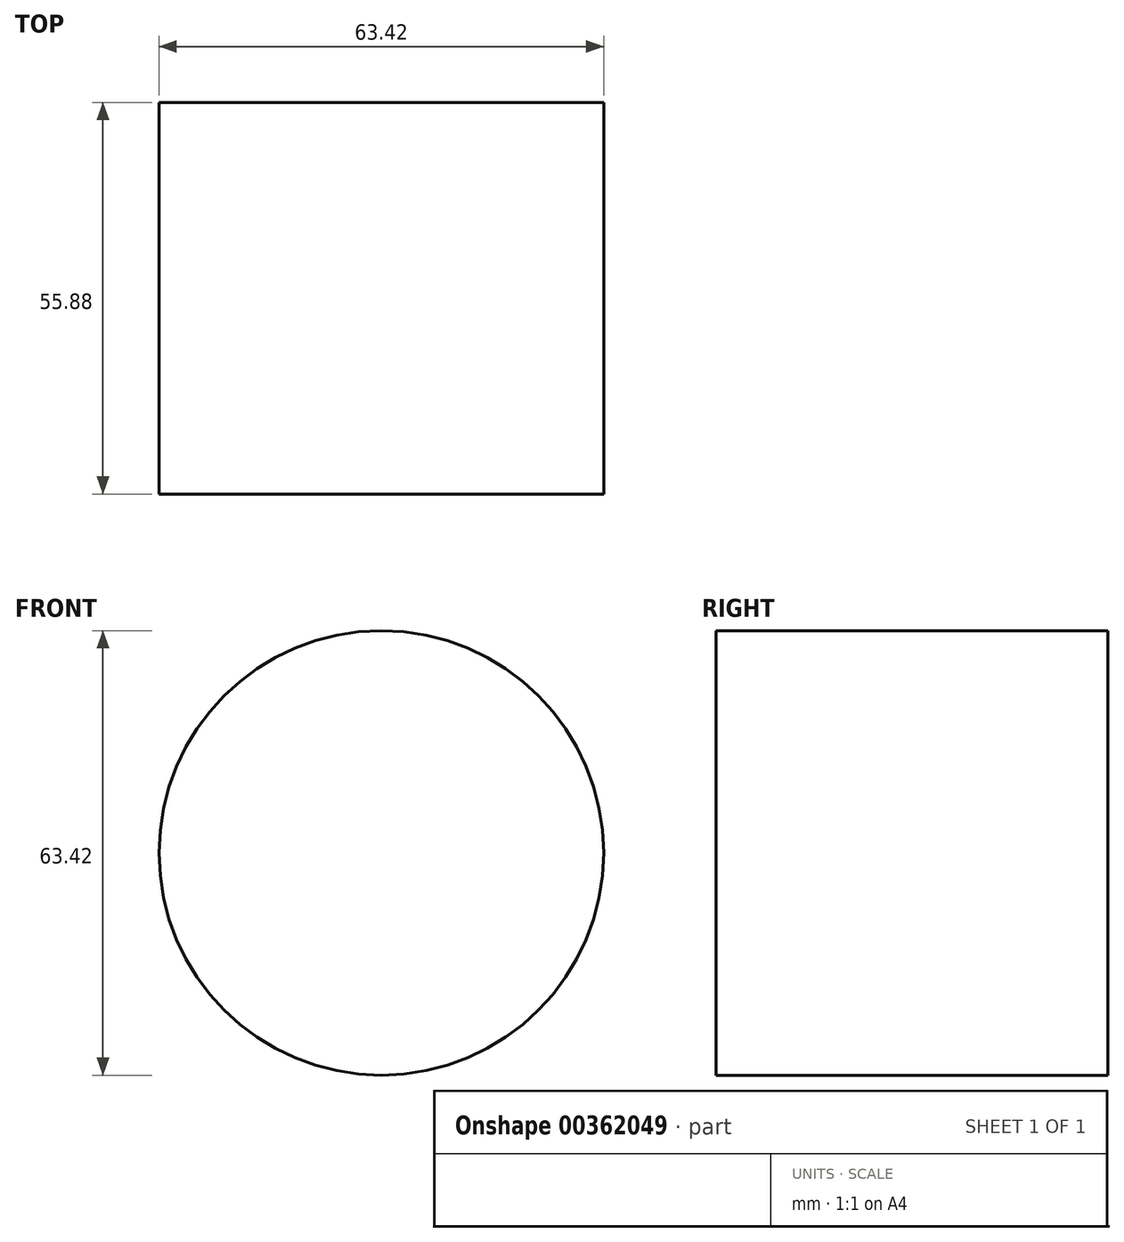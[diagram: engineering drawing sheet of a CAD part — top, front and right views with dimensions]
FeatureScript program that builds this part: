
annotation { "Feature Type Name" : "Feature", "Feature Type Description" : "" }
export const myFeature = defineFeature(function(context is Context, id is Id, definition is map)
    precondition{}
    {
        {
            var Q0;
            Q0=qCreatedBy(makeId("Front.planeOp"),FACE);
            var sketch = newSketch(context, id + "F0", { "sketchPlane" : qUnion([Q0])});
            skCircle(sketch, "E0", {"center": v(0, 0) * mm, "radius": 31.7 * mm});
            skSolve(sketch);
        }
        {
            var Q0;
            Q0 = qSketchRegion(id + "F0", true);
            extrude(context, id + "F1", {"entities" : qUnion([Q0]), "depth" : 55.88 * mm});
        }
    });
